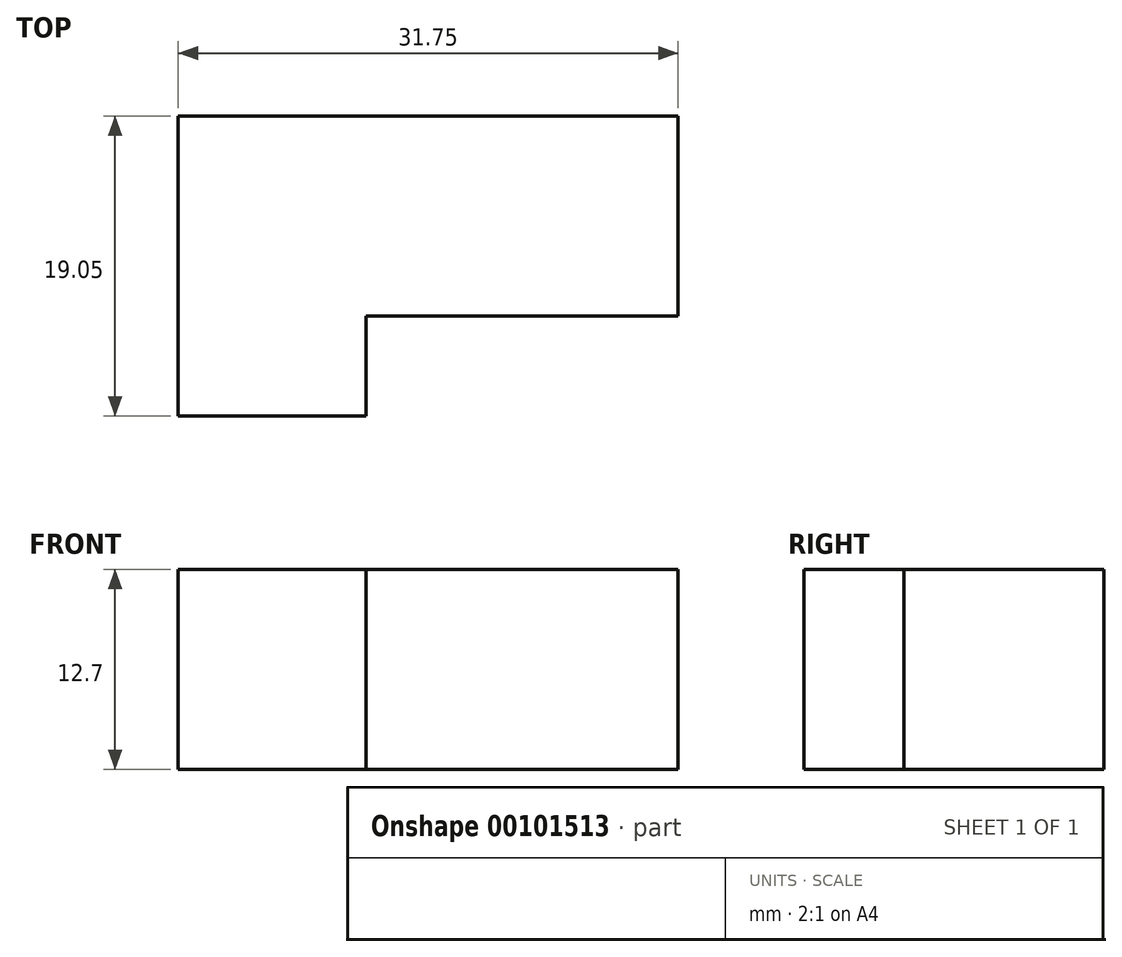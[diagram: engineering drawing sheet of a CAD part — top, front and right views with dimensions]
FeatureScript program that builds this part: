
annotation { "Feature Type Name" : "Feature", "Feature Type Description" : "" }
export const myFeature = defineFeature(function(context is Context, id is Id, definition is map)
    precondition{}
    {
        {
            var Q0;
            Q0=qCreatedBy(makeId("Front.planeOp"),FACE);
            var sketch = newSketch(context, id + "F0", { "sketchPlane" : qUnion([Q0])});
            skLineSegment(sketch, "E0.bottom", {"start": v(0, 0) * mm, "end": v(38.1, 0) * mm});
            skLineSegment(sketch, "E0.top", {"start": v(0, -25.4) * mm, "end": v(38.1, -25.4) * mm});
            skLineSegment(sketch, "E0.left", {"start": v(0, 0) * mm, "end": v(0, -25.4) * mm});
            skLineSegment(sketch, "E0.right", {"start": v(38.1, 0) * mm, "end": v(38.1, -25.4) * mm});
            skLineSegment(sketch, "E1.bottom", {"start": v(38.1, 0) * mm, "end": v(6.35, 0) * mm});
            skLineSegment(sketch, "E1.top", {"start": v(38.1, -12.7) * mm, "end": v(6.35, -12.7) * mm});
            skLineSegment(sketch, "E1.left", {"start": v(38.1, 0) * mm, "end": v(38.1, -12.7) * mm});
            skLineSegment(sketch, "E1.right", {"start": v(6.35, 0) * mm, "end": v(6.35, -12.7) * mm});
            skSolve(sketch);
        }
        {
            var Q0;
            Q0=makeQuery(id+"F0.imprint","IMPRINT",FACE,{"disambiguationData":[TD([[makeQuery(id+"F0.imprint","IMPRINT",EDGE,{"derivedFrom":sQuery(id+"F0.wireOp",EDGE,"E0.bottom")}),-1.0]])]});
            extrude(context, id + "F1", {"entities" : qUnion([Q0]), "depth" : 25.4 * mm});
        }
        {
            var Q0;
            Q0=qCreatedBy(makeId("Top.planeOp"),FACE);
            var sketch = newSketch(context, id + "F2", { "sketchPlane" : qUnion([Q0])});
            skLineSegment(sketch, "E2.bottom", {"start": v(-0.77, 0) * mm, "end": v(18.28, 0) * mm});
            skLineSegment(sketch, "E2.top", {"start": v(-0.77, -12.7) * mm, "end": v(18.28, -12.7) * mm});
            skLineSegment(sketch, "E2.left", {"start": v(-0.77, 0) * mm, "end": v(-0.77, -12.7) * mm});
            skLineSegment(sketch, "E2.right", {"start": v(18.28, 0) * mm, "end": v(18.28, -12.7) * mm});
            skLineSegment(sketch, "E3.bottom", {"start": v(18.28, -12.7) * mm, "end": v(39.14, -12.7) * mm});
            skLineSegment(sketch, "E3.top", {"start": v(18.28, -26.2) * mm, "end": v(39.14, -26.2) * mm});
            skLineSegment(sketch, "E3.left", {"start": v(18.28, -12.7) * mm, "end": v(18.28, -26.2) * mm});
            skLineSegment(sketch, "E3.right", {"start": v(39.14, -12.7) * mm, "end": v(39.14, -26.2) * mm});
            skSolve(sketch);
        }
        {
            var Q0;
            Q0=makeQuery(id+"F2.imprint","IMPRINT",FACE,{"disambiguationData":[TD([[makeQuery(id+"F2.imprint","IMPRINT",EDGE,{"derivedFrom":sQuery(id+"F2.wireOp",EDGE,"E3.bottom")}),-1.0]])]});
            extrude(context, id + "F3", {"entities" : qUnion([Q0]), "operationType" : NewBodyOperationType.REMOVE, "endBound" : BoundingType.THROUGH_ALL, "oppositeDirection" : true, "depth" : 25.4 * mm});
        }
        {
            var Q0;
            Q0=qCreatedBy(makeId("Right.planeOp"),FACE);
            var sketch = newSketch(context, id + "F4", { "sketchPlane" : qUnion([Q0])});
            skLineSegment(sketch, "E4.bottom", {"start": v(0, 0) * mm, "end": v(-19.05, 0) * mm});
            skLineSegment(sketch, "E4.top", {"start": v(0, -12.9) * mm, "end": v(-19.05, -12.9) * mm});
            skLineSegment(sketch, "E4.left", {"start": v(0, 0) * mm, "end": v(0, -12.9) * mm});
            skLineSegment(sketch, "E4.right", {"start": v(-19.05, 0) * mm, "end": v(-19.05, -12.9) * mm});
            skLineSegment(sketch, "E5.bottom", {"start": v(-19.05, 0) * mm, "end": v(-27.02, 0) * mm});
            skLineSegment(sketch, "E5.top", {"start": v(-19.05, -12.7) * mm, "end": v(-27.02, -12.7) * mm});
            skLineSegment(sketch, "E5.left", {"start": v(-19.05, 0) * mm, "end": v(-19.05, -12.7) * mm});
            skLineSegment(sketch, "E5.right", {"start": v(-27.02, 0) * mm, "end": v(-27.02, -12.7) * mm});
            skSolve(sketch);
        }
        {
            var Q0;
            Q0=makeQuery(id+"F4.imprint","IMPRINT",FACE,{"disambiguationData":[TD([[makeQuery(id+"F4.imprint","IMPRINT",EDGE,{"derivedFrom":sQuery(id+"F4.wireOp",EDGE,"E5.bottom")}),1.0]])]});
            extrude(context, id + "F5", {"entities" : qUnion([Q0]), "operationType" : NewBodyOperationType.REMOVE, "depth" : 25.4 * mm});
        }
    });
